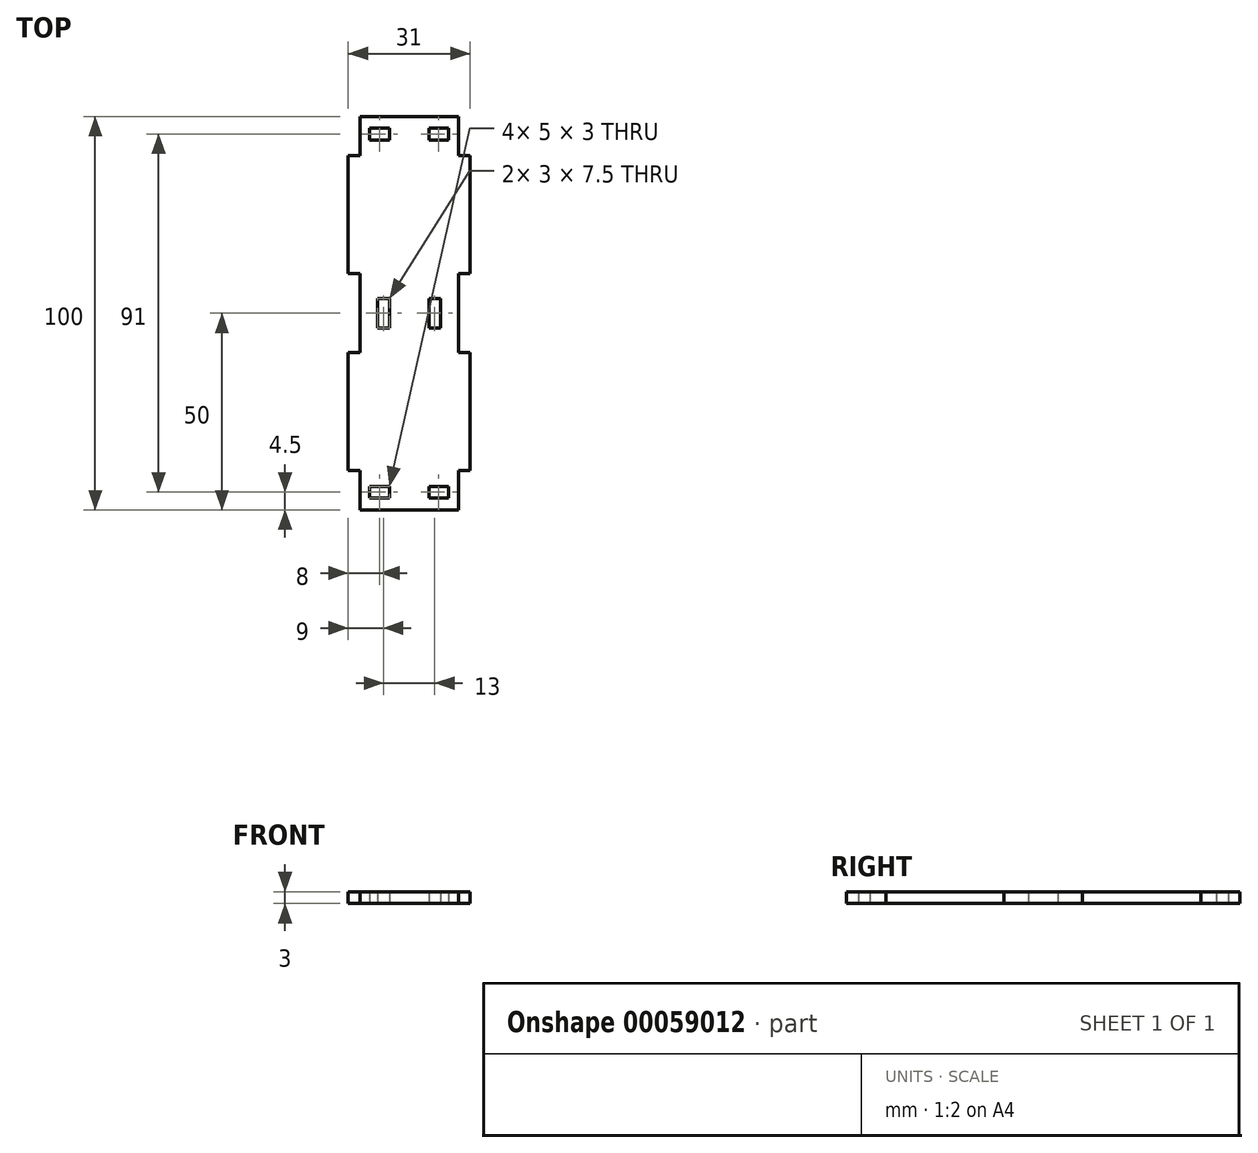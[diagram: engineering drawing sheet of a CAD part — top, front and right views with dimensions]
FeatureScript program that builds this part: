
annotation { "Feature Type Name" : "Feature", "Feature Type Description" : "" }
export const myFeature = defineFeature(function(context is Context, id is Id, definition is map)
    precondition{}
    {
        {
            var Q0;
            Q0=qCreatedBy(makeId("Top.planeOp"),FACE);
            var sketch = newSketch(context, id + "F0", { "sketchPlane" : qUnion([Q0])});
            skLineSegment(sketch, "E0.rect.left", {"start": v(-12.5, 50) * mm, "end": v(-12.5, 40) * mm});
            skPoint(sketch, "E0.rect.middle", {"position": v(0, 0) * mm});
            skLineSegment(sketch, "E1.bottom", {"start": v(-12.5, 40) * mm, "end": v(-15.5, 40) * mm});
            skLineSegment(sketch, "E1.top", {"start": v(-12.5, 10) * mm, "end": v(-15.5, 10) * mm});
            skLineSegment(sketch, "E1.right", {"start": v(-15.5, 40) * mm, "end": v(-15.5, 10) * mm});
            skLineSegment(sketch, "E2", {"start": v(-12.5, 0) * mm, "end": v(12.5, 0) * mm, "construction": true});
            skLineSegment(sketch, "E3.trimOffspring", {"start": v(-12.5, 10) * mm, "end": v(-12.5, -10) * mm});
            skLineSegment(sketch, "E4.MirrorCS", {"start": v(15.5, 40) * mm, "end": v(15.5, 10) * mm});
            skLineSegment(sketch, "E5.MirrorCS", {"start": v(12.5, 40) * mm, "end": v(15.5, 40) * mm});
            skLineSegment(sketch, "E6.MirrorCS", {"start": v(12.5, 10) * mm, "end": v(15.5, 10) * mm});
            skLineSegment(sketch, "E7.MirrorCS", {"start": v(12.5, -40) * mm, "end": v(15.5, -40) * mm});
            skLineSegment(sketch, "E8.MirrorCS", {"start": v(15.5, -40) * mm, "end": v(15.5, -10) * mm});
            skLineSegment(sketch, "E9.MirrorCS", {"start": v(12.5, -10) * mm, "end": v(15.5, -10) * mm});
            skLineSegment(sketch, "E10.MirrorCS", {"start": v(-12.5, -10) * mm, "end": v(-15.5, -10) * mm});
            skLineSegment(sketch, "E11.MirrorCS", {"start": v(-15.5, -40) * mm, "end": v(-15.5, -10) * mm});
            skLineSegment(sketch, "E12.MirrorCS", {"start": v(-12.5, -40) * mm, "end": v(-15.5, -40) * mm});
            skLineSegment(sketch, "E13.trimOffspring", {"start": v(12.5, 10) * mm, "end": v(12.5, -10) * mm});
            skLineSegment(sketch, "E14.trimOffspring", {"start": v(12.5, -40) * mm, "end": v(12.5, -50) * mm});
            skLineSegment(sketch, "E15.trimOffspring", {"start": v(-12.5, -40) * mm, "end": v(-12.5, -50) * mm});
            skLineSegment(sketch, "E16", {"start": v(12.5, 50) * mm, "end": v(12.5, 40) * mm});
            skLineSegment(sketch, "E17.rect.bottom", {"start": v(5, 3.75) * mm, "end": v(8, 3.75) * mm});
            skLineSegment(sketch, "E17.rect.top", {"start": v(5, -3.75) * mm, "end": v(8, -3.75) * mm});
            skLineSegment(sketch, "E17.rect.left", {"start": v(5, 3.75) * mm, "end": v(5, -3.75) * mm});
            skLineSegment(sketch, "E17.rect.right", {"start": v(8, 3.75) * mm, "end": v(8, -3.75) * mm});
            skPoint(sketch, "E17.rect.middle", {"position": v(6.5, 0) * mm});
            skPoint(sketch, "E18.MirrorP", {"position": v(-6.5, 0) * mm});
            skLineSegment(sketch, "E19.MirrorCS", {"start": v(-5, 3.75) * mm, "end": v(-5, -3.75) * mm});
            skLineSegment(sketch, "E20.MirrorCS", {"start": v(-5, -3.75) * mm, "end": v(-8, -3.75) * mm});
            skLineSegment(sketch, "E21.MirrorCS", {"start": v(-8, 3.75) * mm, "end": v(-8, -3.75) * mm});
            skLineSegment(sketch, "E22.MirrorCS", {"start": v(-5, 3.75) * mm, "end": v(-8, 3.75) * mm});
            skLineSegment(sketch, "E23.bottom", {"start": v(-10, 47) * mm, "end": v(-5, 47) * mm});
            skLineSegment(sketch, "E23.top", {"start": v(-10, 44) * mm, "end": v(-5, 44) * mm});
            skLineSegment(sketch, "E23.left", {"start": v(-10, 47) * mm, "end": v(-10, 44) * mm});
            skLineSegment(sketch, "E23.right", {"start": v(-5, 47) * mm, "end": v(-5, 44) * mm});
            skLineSegment(sketch, "E24", {"start": v(-12.5, 50) * mm, "end": v(12.5, 50) * mm});
            skLineSegment(sketch, "E25", {"start": v(-12.5, -50) * mm, "end": v(12.5, -50) * mm});
            skLineSegment(sketch, "E26.MirrorCS", {"start": v(5, 47) * mm, "end": v(5, 44) * mm});
            skLineSegment(sketch, "E27.MirrorCS", {"start": v(10, 47) * mm, "end": v(10, 44) * mm});
            skLineSegment(sketch, "E28.MirrorCS", {"start": v(10, 47) * mm, "end": v(5, 47) * mm});
            skLineSegment(sketch, "E29.MirrorCS", {"start": v(10, 44) * mm, "end": v(5, 44) * mm});
            skLineSegment(sketch, "E30.MirrorCS", {"start": v(-10, -47) * mm, "end": v(-5, -47) * mm});
            skLineSegment(sketch, "E31.MirrorCS", {"start": v(10, -47) * mm, "end": v(5, -47) * mm});
            skLineSegment(sketch, "E32.MirrorCS", {"start": v(-10, -47) * mm, "end": v(-10, -44) * mm});
            skLineSegment(sketch, "E33.MirrorCS", {"start": v(-10, -44) * mm, "end": v(-5, -44) * mm});
            skLineSegment(sketch, "E34.MirrorCS", {"start": v(-5, -47) * mm, "end": v(-5, -44) * mm});
            skLineSegment(sketch, "E35.MirrorCS", {"start": v(10, -47) * mm, "end": v(10, -44) * mm});
            skLineSegment(sketch, "E36.MirrorCS", {"start": v(10, -44) * mm, "end": v(5, -44) * mm});
            skLineSegment(sketch, "E37.MirrorCS", {"start": v(5, -47) * mm, "end": v(5, -44) * mm});
            skSolve(sketch);
        }
        {
            var Q0;
            Q0=makeQuery(id+"F0.imprint","IMPRINT",FACE,{"disambiguationData":[TD([[makeQuery(id+"F0.imprint","IMPRINT",EDGE,{"derivedFrom":sQuery(id+"F0.wireOp",EDGE,"E0.rect.left")}),1.0]])]});
            extrude(context, id + "F1", {"entities" : qUnion([Q0]), "depth" : 3 * mm});
        }
    });
